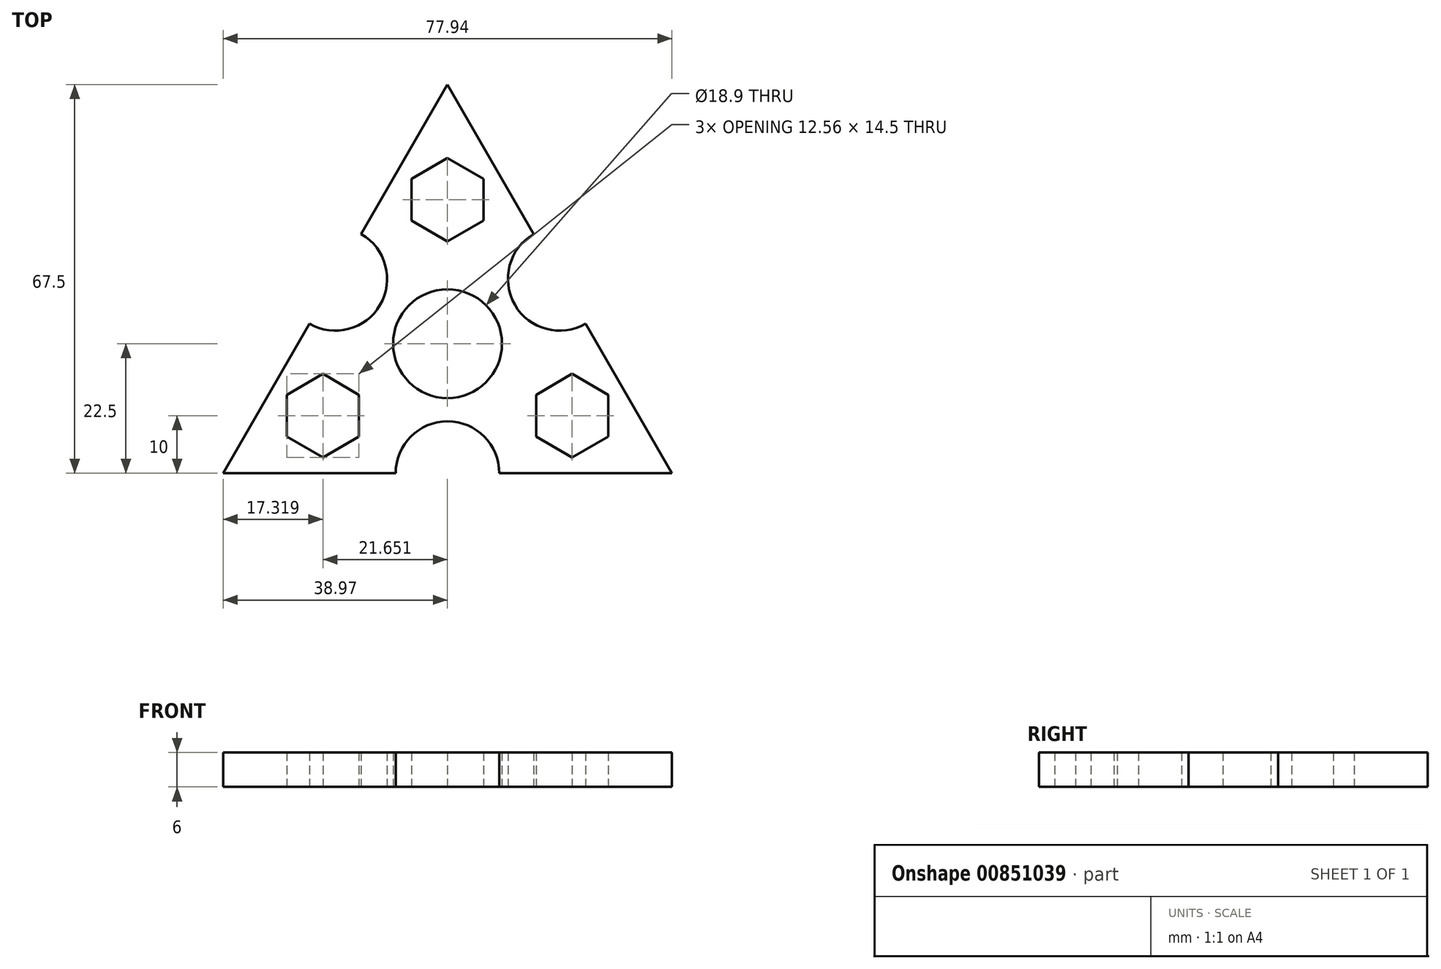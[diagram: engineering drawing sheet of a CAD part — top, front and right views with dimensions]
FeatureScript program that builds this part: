
annotation { "Feature Type Name" : "Feature", "Feature Type Description" : "" }
export const myFeature = defineFeature(function(context is Context, id is Id, definition is map)
    precondition{}
    {
        {
            var Q0;
            Q0=qCreatedBy(makeId("Top.planeOp"),FACE);
            var sketch = newSketch(context, id + "F0", { "sketchPlane" : qUnion([Q0])});
            skCircle(sketch, "E0", {"center": v(0, 0) * mm, "radius": 45 * mm, "construction": true});
            skLineSegment(sketch, "E1.0", {"start": v(0, 45) * mm, "end": v(38.97, -22.5) * mm});
            skLineSegment(sketch, "E1.1", {"start": v(38.97, -22.5) * mm, "end": v(-38.97, -22.5) * mm});
            skLineSegment(sketch, "E1.2", {"start": v(-38.97, -22.5) * mm, "end": v(0, 45) * mm});
            skLineSegment(sketch, "E2", {"start": v(0, 45) * mm, "end": v(0, -22.5) * mm, "construction": true});
            skLineSegment(sketch, "E3.1.0", {"start": v(-38.97, -22.5) * mm, "end": v(19.49, 11.25) * mm, "construction": true});
            skLineSegment(sketch, "E3.2.0", {"start": v(38.97, -22.5) * mm, "end": v(-19.49, 11.25) * mm, "construction": true});
            skArc(sketch, "E4", {"start": v(14.99, 19.04) * mm, "mid": v(11.7, 6.75) * mm, "end": v(23.99, 3.46) * mm});
            skCircle(sketch, "E5", {"center": v(0, 0) * mm, "radius": 9.45 * mm});
            skPoint(sketch, "E6.center", {"position": v(-8.35, -4.82) * mm});
            skArc(sketch, "E7.1.0", {"start": v(-23.99, 3.46) * mm, "mid": v(-11.7, 6.75) * mm, "end": v(-14.99, 19.04) * mm});
            skArc(sketch, "E7.2.0", {"start": v(9, -22.5) * mm, "mid": v(0, -13.5) * mm, "end": v(-9, -22.5) * mm});
            skPoint(sketch, "E8", {"position": v(0, 25) * mm});
            skCircle(sketch, "E9.cCircle", {"center": v(0, 25) * mm, "radius": 7.25 * mm, "construction": true});
            skLineSegment(sketch, "E9.0", {"start": v(0, 32.25) * mm, "end": v(6.28, 28.63) * mm});
            skLineSegment(sketch, "E9.1", {"start": v(6.28, 28.62) * mm, "end": v(6.28, 21.37) * mm});
            skLineSegment(sketch, "E9.2", {"start": v(6.28, 21.37) * mm, "end": v(0, 17.75) * mm});
            skLineSegment(sketch, "E9.3", {"start": v(0, 17.75) * mm, "end": v(-6.28, 21.37) * mm});
            skLineSegment(sketch, "E9.4", {"start": v(-6.28, 21.37) * mm, "end": v(-6.28, 28.62) * mm});
            skLineSegment(sketch, "E9.5", {"start": v(-6.28, 28.62) * mm, "end": v(0, 32.25) * mm});
            skPoint(sketch, "E10.center", {"position": v(4.33, 7.5) * mm});
            skLineSegment(sketch, "E11.1.0", {"start": v(-21.65, -19.75) * mm, "end": v(-27.93, -16.12) * mm});
            skLineSegment(sketch, "E11.1.1", {"start": v(-27.93, -16.12) * mm, "end": v(-27.93, -8.87) * mm});
            skLineSegment(sketch, "E11.1.2", {"start": v(-27.93, -8.87) * mm, "end": v(-21.65, -5.25) * mm});
            skLineSegment(sketch, "E11.1.3", {"start": v(-21.65, -5.25) * mm, "end": v(-15.37, -8.87) * mm});
            skLineSegment(sketch, "E11.1.4", {"start": v(-15.37, -8.87) * mm, "end": v(-15.37, -16.12) * mm});
            skLineSegment(sketch, "E11.1.5", {"start": v(-15.37, -16.12) * mm, "end": v(-21.65, -19.75) * mm});
            skLineSegment(sketch, "E11.2.0", {"start": v(27.93, -8.87) * mm, "end": v(27.93, -16.12) * mm});
            skLineSegment(sketch, "E11.2.1", {"start": v(27.93, -16.13) * mm, "end": v(21.65, -19.75) * mm});
            skLineSegment(sketch, "E11.2.2", {"start": v(21.65, -19.75) * mm, "end": v(15.37, -16.13) * mm});
            skLineSegment(sketch, "E11.2.3", {"start": v(15.37, -16.13) * mm, "end": v(15.37, -8.87) * mm});
            skLineSegment(sketch, "E11.2.4", {"start": v(15.37, -8.87) * mm, "end": v(21.65, -5.25) * mm});
            skLineSegment(sketch, "E11.2.5", {"start": v(21.65, -5.25) * mm, "end": v(27.93, -8.87) * mm});
            skSolve(sketch);
        }
        {
            var Q0;
            {var subQ4=sQuery(id+"F0.wireOp",EDGE,"E4");Q0=makeQuery(id+"F0.imprint","IMPRINT",FACE,{"disambiguationData":[TD([[makeQuery(id+"F0.imprint","IMPRINT",EDGE,{"derivedFrom":subQ4}),-1.0]])]});}
            extrude(context, id + "F1", {"entities" : qUnion([Q0]), "depth" : 6 * mm, "offsetDistance" : 25 * mm});
        }
    });
